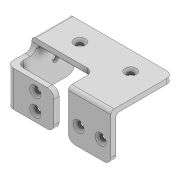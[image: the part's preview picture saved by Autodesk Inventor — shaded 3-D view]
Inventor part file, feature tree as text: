
AUTODESK INVENTOR PART (.ipt)
format: ipt  version: 2021 (Build 250183000, 183)  size: 252,416 bytes
history: native  units: mm
features: sketch x7, projected_geometry x7, extrude x4, hole x3, other x1, fillet x1
ambient origin geometry x8: Origin, YZ Plane, XZ Plane, XY Plane, X Axis, Y Axis, Z Axis, Center Point
bodies: Body1 (feature_tree)
feature tree (23):
  other  "Твердое тело1"
  extrude  "Выдавливание1"  Depth=22.0mm
  extrude  "Выдавливание2"  Depth=58.5mm
  extrude  "Выдавливание3"  Depth=3.0mm TaperAngle=0.0deg
  extrude  "Выдавливание4"  Depth=28.0mm
  fillet  "Сопряжение1"  Radius=3.0mm
  hole  "Отверстие1"  [1 undecoded]
  hole  "Отверстие2"  [1 undecoded]
  hole  "Отверстие3"  [1 undecoded]
  sketch  "Эскиз1"
  sketch  "Эскиз2"
  projected_geometry  "Спроецированная петля1"
  sketch  "Эскиз3"
  projected_geometry  "Спроецированная петля2"
  sketch  "Эскиз4"
  projected_geometry  "Спроецированная петля3"
  sketch  "Эскиз5"
  projected_geometry  "Спроецированная петля4"
  projected_geometry  "Спроецированная петля5"
  sketch  "Эскиз6"
  projected_geometry  "Спроецированная петля6"
  sketch  "Эскиз7"
  projected_geometry  "Спроецированная петля7"
note: 3 required parameter values undecoded (feature->parameter linkage not recoverable at this tier; creation-order binding heuristic only, values carry confidence <= 0.55)
